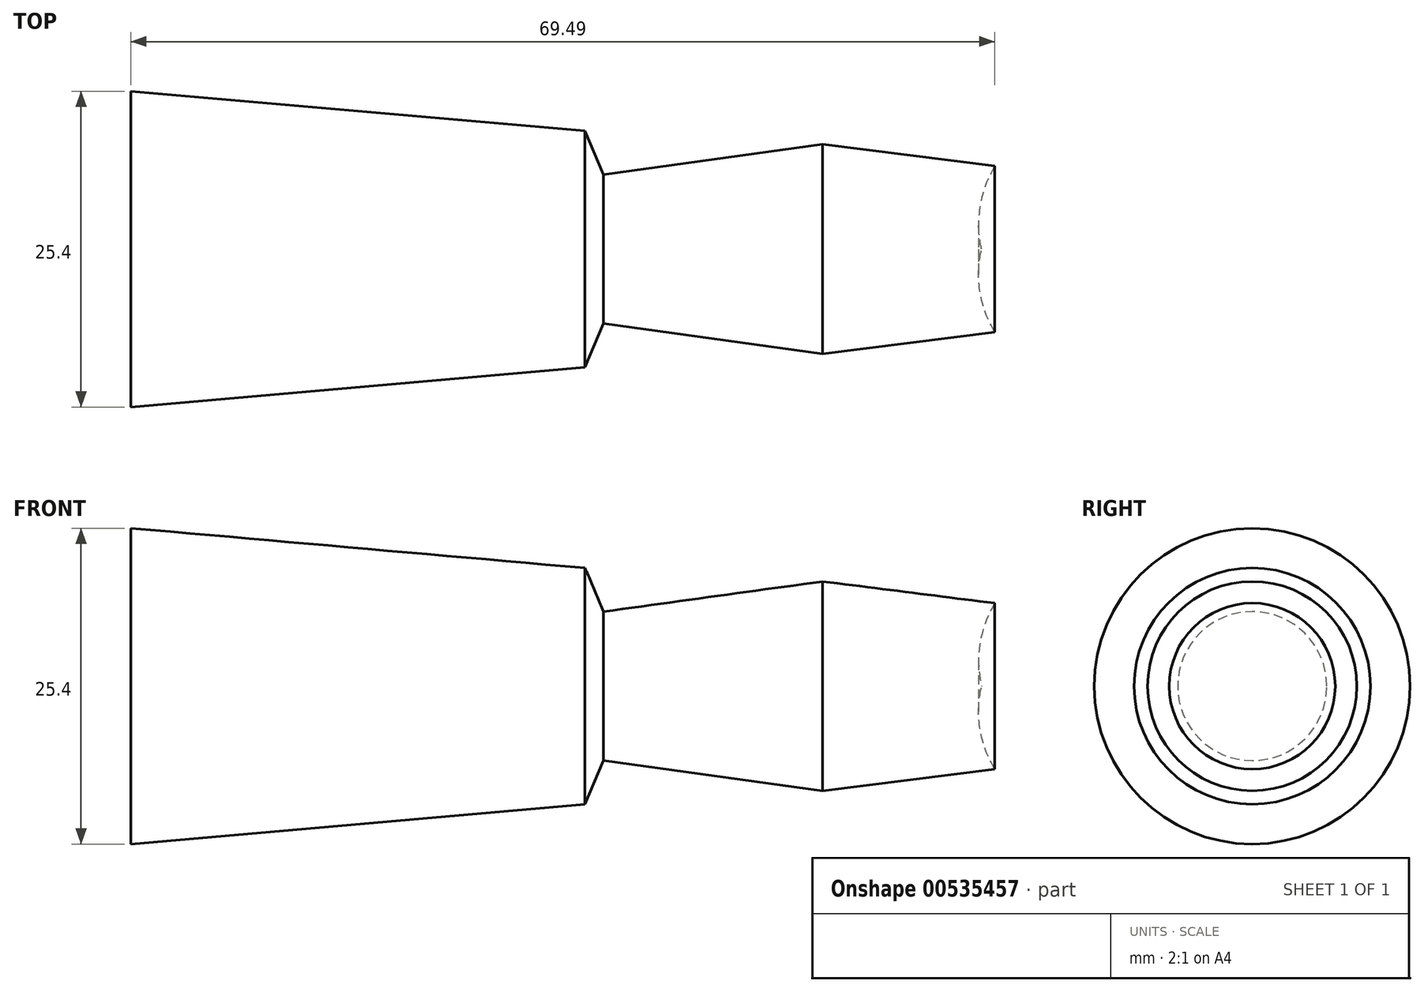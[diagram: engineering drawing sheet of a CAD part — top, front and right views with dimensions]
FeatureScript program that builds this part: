
annotation { "Feature Type Name" : "Feature", "Feature Type Description" : "" }
export const myFeature = defineFeature(function(context is Context, id is Id, definition is map)
    precondition{}
    {
        {
            var Q0;
            Q0=qCreatedBy(makeId("Front.planeOp"),FACE);
            var sketch = newSketch(context, id + "F0", { "sketchPlane" : qUnion([Q0])});
            skLineSegment(sketch, "E0", {"start": v(-85.73, 0) * mm, "end": v(0, 0) * mm});
            skLineSegment(sketch, "E1", {"start": v(-85.73, 0) * mm, "end": v(-85.73, 12.7) * mm});
            skArc(sketch, "E2", {"start": v(0, 0) * mm, "mid": v(-5.27, 10.26) * mm, "end": v(-16.24, 6.67) * mm});
            skLineSegment(sketch, "E3", {"start": v(-85.73, 12.7) * mm, "end": v(-49.2, 9.5) * mm});
            skLineSegment(sketch, "E4", {"start": v(-49.2, 9.5) * mm, "end": v(-47.71, 6) * mm});
            skLineSegment(sketch, "E5", {"start": v(-47.71, 6) * mm, "end": v(-30.1, 8.42) * mm});
            skLineSegment(sketch, "E6", {"start": v(-30.1, 8.42) * mm, "end": v(-16.24, 6.67) * mm});
            skSolve(sketch);
        }
        {
            var Q0;
            {var subQ0=sQuery(id+"F0.wireOp",EDGE,"E1");Q0=makeQuery(id+"F0.imprint","IMPRINT",FACE,{"disambiguationData":[TD([[makeQuery(id+"F0.imprint","IMPRINT",EDGE,{"derivedFrom":subQ0}),-1.0]])]});}
            var Q1;
            Q1=sQuery(id+"F0.wireOp",EDGE,"E0");
            revolve(context, id + "F1", {"entities" : qUnion([Q0]), "axis" : qUnion([Q1]), "revolveType" : RevolveType.FULL});
        }
    });
